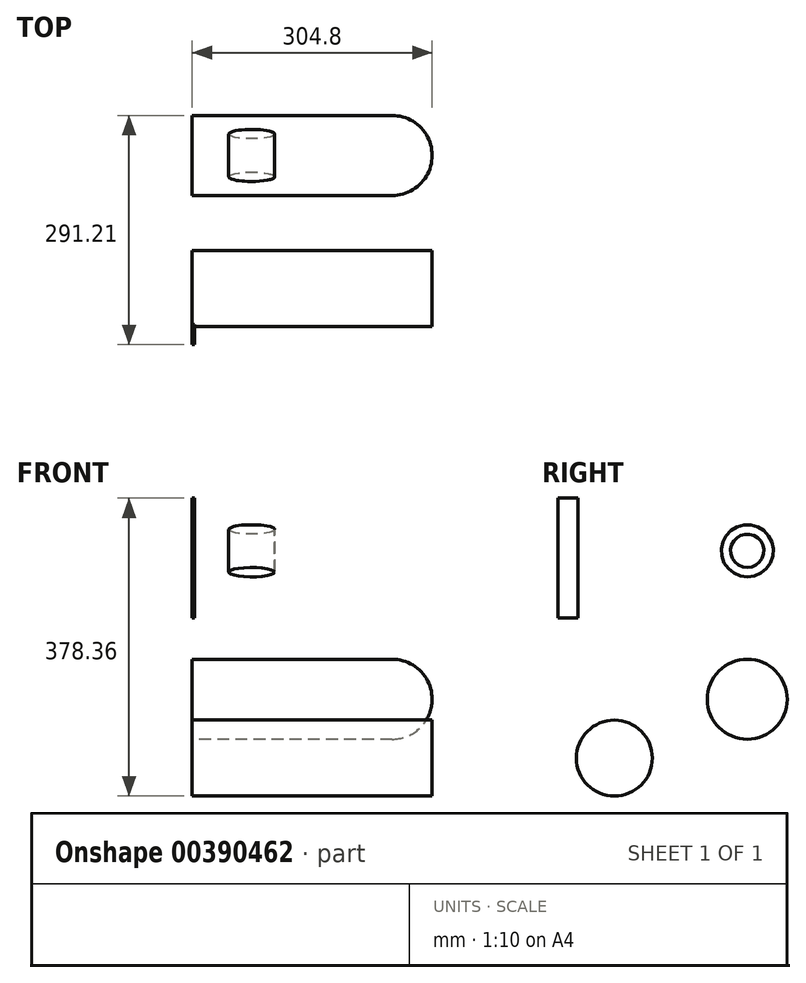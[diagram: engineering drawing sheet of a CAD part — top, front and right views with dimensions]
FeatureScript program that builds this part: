
annotation { "Feature Type Name" : "Feature", "Feature Type Description" : "" }
export const myFeature = defineFeature(function(context is Context, id is Id, definition is map)
    precondition{}
    {
        {
            var Q0;
            Q0=qCreatedBy(makeId("Front.planeOp"),FACE);
            var sketch = newSketch(context, id + "F0", { "sketchPlane" : qUnion([Q0])});
            skLineSegment(sketch, "E0", {"start": v(0, 50.8) * mm, "end": v(254, 50.8) * mm});
            skArc(sketch, "E1", {"start": v(254, 50.8) * mm, "mid": v(289.92, 35.92) * mm, "end": v(304.8, 0) * mm});
            skLineSegment(sketch, "E2", {"start": v(0, 50.8) * mm, "end": v(0, 0) * mm});
            skLineSegment(sketch, "E3", {"start": v(0, 0) * mm, "end": v(304.8, 0) * mm});
            skSolve(sketch);
        }
        {
            var Q0;
            Q0=makeQuery(id+"F0.imprint","IMPRINT",FACE,{"disambiguationData":[TD([[makeQuery(id+"F0.imprint","IMPRINT",EDGE,{"derivedFrom":sQuery(id+"F0.wireOp",EDGE,"E0")}),-1.0]])]});
            var Q1;
            Q1=sQuery(id+"F0.wireOp",EDGE,"E3");
            revolve(context, id + "F1", {"entities" : qUnion([Q0]), "axis" : qUnion([Q1]), "revolveType" : RevolveType.FULL});
        }
        {
            var Q0;
            Q0=qCreatedBy(makeId("Front.planeOp"),FACE);
            var sketch = newSketch(context, id + "F2", { "sketchPlane" : qUnion([Q0])});
            skEllipse(sketch, "E4", {"center": v(75.63, 161.53) * mm, "majorRadius": 29.1 * mm, "minorRadius": 5.95 * mm, "majorAxis": v(1, 0)});
            skLineSegment(sketch, "E5", {"start": v(50.53, 188.66) * mm, "end": v(102.1, 188.66) * mm});
            skSolve(sketch);
        }
        {
            var Q0;
            Q0=makeQuery(id+"F2.imprint","IMPRINT",FACE,{"disambiguationData":[TD([[makeQuery(id+"F2.imprint","IMPRINT",EDGE,{"derivedFrom":sQuery(id+"F2.wireOp",EDGE,"E4")}),1.0]])]});
            var Q1;
            Q1=sQuery(id+"F2.wireOp",EDGE,"E5");
            revolve(context, id + "F3", {"entities" : qUnion([Q0]), "axis" : qUnion([Q1]), "revolveType" : RevolveType.FULL});
        }
        {
            var Q0;
            Q0=qCreatedBy(makeId("Right.planeOp"),FACE);
            var sketch = newSketch(context, id + "F4", { "sketchPlane" : qUnion([Q0])});
            skCircle(sketch, "E6", {"center": v(-168.83, -74.68) * mm, "radius": 48.23 * mm});
            skSolve(sketch);
        }
        {
            var Q0;
            Q0 = qSketchRegion(id + "F4", true);
            extrude(context, id + "F5", {"entities" : qUnion([Q0]), "depth" : 304.8 * mm});
        }
        {
            var Q0;
            Q0=qCreatedBy(makeId("Right.planeOp"),FACE);
            var sketch = newSketch(context, id + "F6", { "sketchPlane" : qUnion([Q0])});
            skLineSegment(sketch, "E7.bottom", {"start": v(-215, 103.05) * mm, "end": v(-240.4, 103.05) * mm});
            skLineSegment(sketch, "E7.top", {"start": v(-215, 255.45) * mm, "end": v(-240.4, 255.45) * mm});
            skLineSegment(sketch, "E7.left", {"start": v(-215, 103.05) * mm, "end": v(-215, 255.45) * mm});
            skLineSegment(sketch, "E7.right", {"start": v(-240.4, 103.05) * mm, "end": v(-240.4, 255.45) * mm});
            skSolve(sketch);
        }
        {
            var Q0;
            Q0=makeQuery(id+"F6.imprint","IMPRINT",FACE,{"disambiguationData":[TD([[makeQuery(id+"F6.imprint","IMPRINT",EDGE,{"derivedFrom":sQuery(id+"F6.wireOp",EDGE,"E7.bottom")}),-1.0]])]});
            extrude(context, id + "F7", {"entities" : qUnion([Q0]), "depth" : 3.17 * mm});
        }
    });
